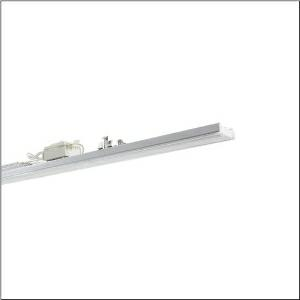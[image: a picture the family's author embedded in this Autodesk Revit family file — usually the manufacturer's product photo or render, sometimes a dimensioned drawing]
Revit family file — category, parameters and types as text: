
# Revit family: licross_r__21_recessed_mo_51te11vn445g_2ea5
name_source: partatom
category: Lighting Fixtures
units: mm (PartAtom-declared; Revit-internal decimal feet)

## family parameters
Cut with Voids When Loaded = No
Host = Face
Light Source = No
Part Type = Normal
Room Calculation Point = No
Round Connector Dimension = Use Diameter
Shared = No

## types (1)
- --- (1 x LED, 4500 lm, 24.3 W, 4000K)
    Apparent Load = 24 VA
    CIE Flux Codes = 89 96 99 100 100
    Color Rendering = 80
    Color Temperature = 4000K
    Default Elevation = 1800 mm
    Description = Licross® 21 Recessed MO, luminaire insert, of sheet steel, galvanised, coil coated, white, length: 1.500mm, width: 66mm, height: 67mm, LED rated luminous flux: 4.500lm, light colour: 840, control gear: DALI 2, CLO, with plug, 5-pole, with phase selection, mains connection: 220..240V, AC, 50/60Hz, start of lifetime: 24W, end of service life: 26W, halogen-free wiring, primary light control with lens, of plastic, primary optical cover: cover, of PMMA, light emission: direct distribution, primary light characteristic: symmetric, protection rating (complete): IP54, insulation class (complete): insulation class I (protective earthing), certification: CE, ENEC, VDE, UKCA, protection symbol: D if used in an environment with non-conductive dust loads with corresponding accessories, impact resistance: IK06, permissible ambient temperature for indoor applications: -25..+45°C, corresponds to IFS (International Featured Standards) requirements for safety and quality in the food industry, reducing of maximum allowable ambient temperature of 5°C with ceiling mounting, LABS conformity tested according to VDMA 24364:2018-05, packaging unit: 1 piece
    Height = 58 mm
    Lamp = 1 x LED
    Lamp Light Flux = 4500 lm
    Lamp Power = 24.3 W
    Lamp count = 1
    Length = 1500 mm
    Luminous efficacy = 185 lm/W
    Manufacturer = Siteco
    ModVariant = No
    Model = 51TE11VN445G
    Mounting Place = Ceiling
    Mounting Type = Pendant
    Number of Poles = 1
    OnlyDefault = Yes
    Power Factor = 1
    Product Name = Licross® 21 Recessed MO
    Product group = luminaire insert
    ProductGroupID = 902
    Protection Class = Protection class I
    Protection Degree = IP 54
    RLX_Detail_Level = 1
    RLX_Emergency_Light_Flux = 0 lm
    RLX_Emergency_Type = 0
    RLX_Emergency_Type_DB = No
    RlxData = <blob elided: 24189 chars, md5=b8974713>
    Socket = socket
    Standby Power = 0 W
    System Light Flux = 4500 lm
    System Power = 24 W
    Type Comments = factory setting: luminous flux: 100 % | dim-lin: 254 | 160 mA
    Type Image = l_1296930.jpg
    URL = http://relux.com
    VarID = @adj_086974
    Voltage = 0 V
    Weight = 0.00 kg
    Width = 66 mm

## geometry (parser evidence)
native form markers: Blend x4, Sweep x12
no freeform markers — native parametric forms only
